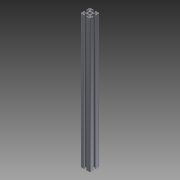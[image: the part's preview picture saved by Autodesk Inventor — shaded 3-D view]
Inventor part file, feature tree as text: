
AUTODESK INVENTOR PART (.ipt)
format: ipt  version: 2016 (Build 200138000, 138)  size: 214,016 bytes
history: native  units: mm
features: other x42, sketch x5, hole x4, extrude x1
ambient origin geometry x8: Origin, YZ Plane, XZ Plane, XY Plane, X Axis, Y Axis, Z Axis, Center Point
bodies: Solid1 (feature_tree)
feature tree (52):
  extrude  "Extrusion1"  [1 undecoded]
  hole  "Drilling 1"  [1 undecoded]
  hole  "Drilling 2"  [1 undecoded]
  hole  "Drilling 3"  [1 undecoded]
  hole  "Drilling 4"  [1 undecoded]
  other  "side_4d_XY"
  other  "side_4d_YZ"
  other  "side_4d_ZX"
  other  "side_4d_X"
  other  "side_4d_Y"
  other  "side_4d_Z"
  other  "side_4d_Center"
  other  "side_1a_XY"
  other  "side_1a_YZ"
  other  "side_1a_ZX"
  other  "side_1a_X"
  other  "side_1a_Y"
  other  "side_1a_Z"
  other  "side_1a_Center"
  other  "side_2b_XY"
  other  "side_2b_YZ"
  other  "side_2b_ZX"
  other  "side_2b_X"
  other  "side_2b_Y"
  other  "side_2b_Z"
  other  "side_2b_Center"
  other  "side_3c_XY"
  other  "side_3c_YZ"
  other  "side_3c_ZX"
  other  "side_3c_X"
  other  "side_3c_Y"
  other  "side_3c_Z"
  other  "side_3c_Center"
  other  "end_XY"
  other  "end_YZ"
  other  "end_ZX"
  other  "end_X"
  other  "end_Y"
  other  "end_Z"
  other  "end_Center"
  other  "start_XY"
  other  "start_YZ"
  other  "start_ZX"
  other  "start_X"
  other  "start_Y"
  other  "start_Z"
  other  "start_Center"
  sketch  "Skizze_1"  dims[d0=572.0mm d1=0.0mm]
  sketch  "Sketch2"  dims[d2=5.0mm d3=6.0mm d4=4.0mm d5=2.0mm d6=90.0deg d7=6000.0mm d8=0.0mm]
  sketch  "Sketch3"  dims[d9=5.0mm d10=6.0mm d11=4.0mm d12=2.0mm d13=90.0deg d14=6000.0mm d15=0.0mm]
  sketch  "Sketch4"  dims[d16=5.0mm d17=6.0mm d18=4.0mm d19=2.0mm d20=90.0deg d21=6000.0mm d22=0.0mm]
  sketch  "Sketch5"  dims[d23=5.0mm d24=6.0mm d25=4.0mm d26=2.0mm d27=90.0deg d28=6000.0mm d29=0.0mm]
note: 5 required parameter values undecoded (feature->parameter linkage not recoverable at this tier; creation-order binding heuristic only, values carry confidence <= 0.55)
